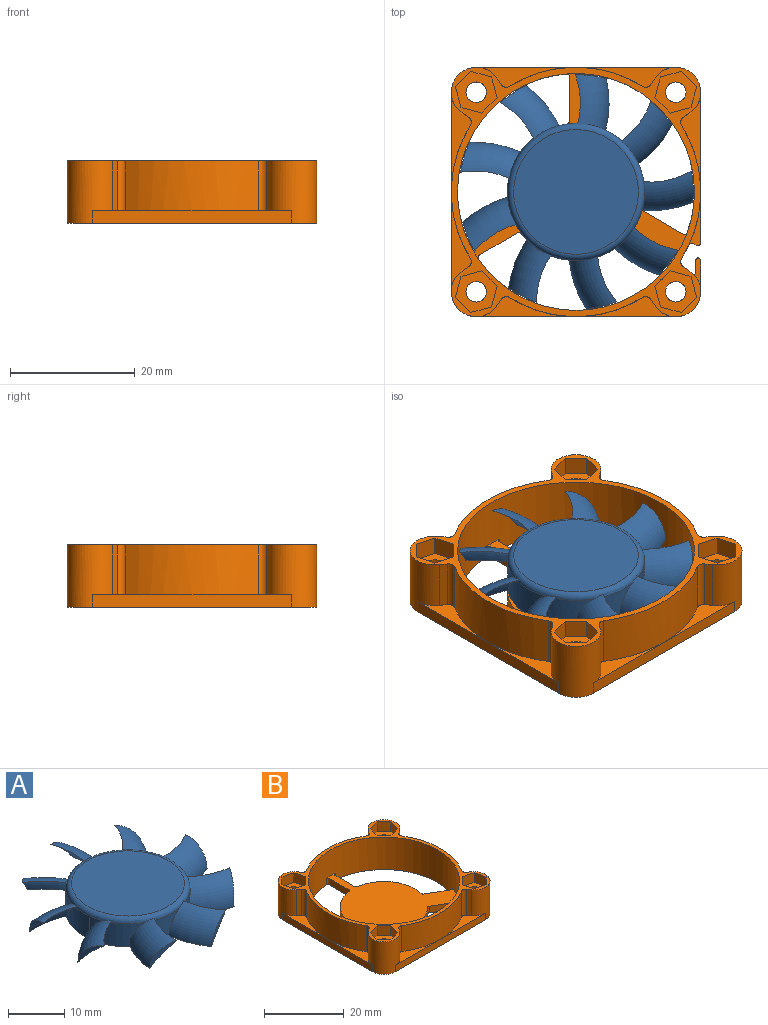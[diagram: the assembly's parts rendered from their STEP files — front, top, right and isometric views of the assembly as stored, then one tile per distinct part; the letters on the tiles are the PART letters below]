
ASSEMBLY  parts=2 mates=1
PART A: 32 faces, bbox 42.3x42.5x6 mm
  f0: cylinder r=11mm len=22mm, axis (0,0,-1), area 307.6mm2, adj f1,f3,f4,f5,f6,f8,f9,f11
  f1: cylinder r=11mm len=4.52mm, axis (0,0,-1), area 3.9mm2, adj f0,f4,f11
  f2: plane 20x20mm, normal (0,0,1), area 314.2mm2, adj f4
  f3: plane 22x22mm, normal (0,0,-1), area 380.1mm2, adj f0
  f4: torus R=10mm, axis (0,0,1), area 102.2mm2, adj f0,f1,f2,f5,f6,f8,f9,f11
  f5: torus R=12.73mm, axis (0,0,-1), area 60.3mm2, adj f0,f4,f6,f7
  f6: torus R=5.4mm, axis (0,0,-1), area 55.4mm2, adj f0,f4,f5,f7
  f7: cylinder r=18.8mm len=4.97mm, axis (0,0,1), area 4.5mm2, adj f5,f6
  f8: torus R=12.73mm, axis (0,0,-1), area 60.3mm2, adj f0,f4,f9,f10
  f9: torus R=5.4mm, axis (0,0,-1), area 55.4mm2, adj f0,f4,f8,f10
  f10: cylinder r=18.8mm len=4.97mm, axis (0,0,1), area 4.5mm2, adj f8,f9
  f11: torus R=12.73mm, axis (0,0,-1), area 60.3mm2, adj f0,f1,f4,f12,f13
  f12: torus R=5.4mm, axis (0,0,-1), area 55.4mm2, adj f0,f4,f11,f13
  f13: cylinder r=18.8mm len=4.97mm, axis (0,0,1), area 4.5mm2, adj f11,f12
  f14: torus R=12.73mm, axis (0,0,-1), area 60.3mm2, adj f0,f4,f15,f16
  f15: torus R=5.4mm, axis (0,0,-1), area 55.4mm2, adj f0,f4,f14,f16
  f16: cylinder r=18.8mm len=4.97mm, axis (0,0,1), area 4.5mm2, adj f14,f15
  f17: torus R=12.73mm, axis (0,0,-1), area 60.3mm2, adj f0,f4,f18,f19
  f18: torus R=5.4mm, axis (0,0,-1), area 55.4mm2, adj f0,f4,f17,f19
  f19: cylinder r=18.8mm len=4.97mm, axis (0,0,1), area 4.5mm2, adj f17,f18
  f20: torus R=12.73mm, axis (0,0,-1), area 60.3mm2, adj f0,f4,f21,f22
  f21: torus R=5.4mm, axis (0,0,-1), area 55.4mm2, adj f0,f4,f20,f22
  f22: cylinder r=18.8mm len=4.99mm, axis (0,0,1), area 4.5mm2, adj f20,f21
  f23: torus R=12.73mm, axis (0,0,-1), area 60.3mm2, adj f0,f4,f24,f25
  f24: torus R=5.4mm, axis (0,0,-1), area 55.4mm2, adj f0,f4,f23,f25
  f25: cylinder r=18.8mm len=4.97mm, axis (0,0,1), area 4.5mm2, adj f23,f24
  f26: torus R=12.73mm, axis (0,0,-1), area 60.3mm2, adj f0,f4,f27,f28
  f27: torus R=5.4mm, axis (0,0,-1), area 55.4mm2, adj f0,f4,f26,f28
  f28: cylinder r=18.8mm len=5mm, axis (0,0,1), area 4.5mm2, adj f26,f27
  f29: torus R=12.73mm, axis (0,0,-1), area 60.3mm2, adj f0,f4,f30,f31
  f30: torus R=5.4mm, axis (0,0,-1), area 55.4mm2, adj f0,f4,f29,f31
  f31: cylinder r=18.8mm len=4.97mm, axis (0,0,1), area 4.5mm2, adj f29,f30
PART B: 115 faces, bbox 40x40x10 mm
  f0: plane 10.28x5.94mm, normal (0.5,0.87,0), area 11.9mm2, adj f19,f33,f35,f80,f81,f82
  f1: plane 2x1.78mm, normal (-1,0,0), area 3.6mm2, adj f8,f33,f81,f97
  f2: plane 16x3.21mm, normal (0,0,1), area 18mm2, adj f26,f27,f56,f57,f100
  f3: plane 16x3.21mm, normal (0,0,1), area 18mm2, adj f25,f26,f65,f69,f106
  f4: plane 16x3.21mm, normal (0,0,1), area 18mm2, adj f21,f22,f34,f60,f102
  f5: plane 16x3.21mm, normal (0,0,1), area 18mm2, adj f23,f24,f62,f63,f104
  f6: plane 16x3.21mm, normal (0,0,1), area 18mm2, adj f27,f28,f57,f58,f101
  f7: plane 35.04x31.24mm, normal (0,0,1), area 457.1mm2, adj f12,f13,f14,f15,f16,f17,f18,f30
  f8: plane 5.45x1.07mm, normal (0,0,1), area 3mm2, adj f1,f28,f29,f81,f96,f97
  f9: plane 16x3.21mm, normal (0,0,1), area 18mm2, adj f22,f23,f61,f62,f103
  f10: plane 8.58x1.89mm, normal (0,0,1), area 5.1mm2, adj f20,f21,f34,f76,f89
  f11: plane 16x3.21mm, normal (0,0,1), area 18mm2, adj f24,f25,f64,f65,f105
  f12: plane 7.04x2mm, normal (1,0,0), area 14.1mm2, adj f7,f33,f87,f92
  f13: cylinder r=19mm len=38mm, axis (0,0,1), area 1168mm2, adj f7,f33,f71,f83,f84,f85,f86,f87
  f14: plane 6.22x3.59mm, normal (0.5,0.87,0), area 14.4mm2, adj f7,f33,f88,f95
  f15: plane 6.09x3.52mm, normal (0.5,-0.87,0), area 14.1mm2, adj f7,f33,f84,f90
  f16: cylinder r=11mm len=16.31mm, axis (0,0,1), area 36.9mm2, adj f7,f33,f90,f94
  f17: plane 6.09x3.52mm, normal (-0.5,0.87,0), area 14.1mm2, adj f7,f33,f85,f91
  f18: plane 7.04x2mm, normal (-1,0,0), area 14.1mm2, adj f7,f33,f86,f93
  f19: cylinder r=11mm len=3.9mm, axis (0,0,1), area 4.4mm2, adj f0,f20,f33,f35,f77
  f20: plane 8.8x5.08mm, normal (-0.5,-0.87,0), area 6.1mm2, adj f10,f19,f33,f76,f77,f78,f89
  f21: plane 24.08x2mm, normal (1,0,0), area 48.2mm2, adj f4,f10,f22,f33,f89
  f22: cylinder r=4mm len=10mm, axis (0,0,1), area 124.5mm2, adj f4,f9,f21,f23,f33,f60,f61,f71
  f23: plane 32x2mm, normal (0,1,0), area 64mm2, adj f5,f9,f22,f24,f33
  f24: cylinder r=4mm len=10mm, axis (0,0,1), area 124.5mm2, adj f5,f11,f23,f25,f33,f63,f64,f71
  f25: plane 32x2mm, normal (-1,0,0), area 64mm2, adj f3,f11,f24,f26,f33
  f26: cylinder r=4mm len=10mm, axis (0,0,1), area 124.5mm2, adj f2,f3,f25,f27,f33,f56,f69,f71
  f27: plane 32x2mm, normal (0,-1,0), area 64mm2, adj f2,f6,f26,f28,f33
  f28: cylinder r=4mm len=10mm, axis (0,0,1), area 124.9mm2, adj f6,f8,f27,f29,f33,f58,f59,f71
  f29: plane 4.96x2mm, normal (1,0,0), area 9.9mm2, adj f8,f28,f33,f96
  f30: plane 6.22x3.59mm, normal (-0.5,-0.87,0), area 14.4mm2, adj f7,f33,f83,f94
  f31: cylinder r=11mm len=15.12mm, axis (0,0,1), area 40.3mm2, adj f7,f33,f91,f93
  f32: cylinder r=11mm len=13.49mm, axis (0,0,1), area 36.9mm2, adj f7,f33,f92,f95
  f33: plane 40x40mm, normal (0,0,-1), area 793.4mm2, adj f0,f1,f12,f13,f14,f15,f16,f17
  f34: cylinder r=20mm len=21.25mm, axis (0,0,1), area 180.4mm2, adj f4,f10,f71,f76,f79,f98,f102
  f35: plane 9.49x8.4mm, normal (0,0,-1), area 34.2mm2, adj f0,f19,f77,f79,f80
  f36: plane 3.35x3mm, normal (-0.26,-0.97,0), area 10.4mm2, adj f37,f70,f71,f75
  f37: plane 3.35x3mm, normal (-0.97,-0.26,0), area 10.4mm2, adj f36,f38,f71,f75
  f38: plane 3x2.45mm, normal (-0.71,0.71,0), area 10.4mm2, adj f37,f39,f71,f75
  f39: plane 3.35x3mm, normal (0.26,0.97,0), area 10.4mm2, adj f38,f40,f71,f75
  f40: plane 3.35x3mm, normal (0.97,0.26,0), area 10.4mm2, adj f39,f70,f71,f75
  f41: plane 3x2.45mm, normal (-0.71,0.71,0), area 10.4mm2, adj f42,f66,f71,f73
  f42: plane 3.35x3mm, normal (0.26,0.97,0), area 10.4mm2, adj f41,f43,f71,f73
  f43: plane 3.35x3mm, normal (0.97,0.26,0), area 10.4mm2, adj f42,f44,f71,f73
  f44: plane 3x2.45mm, normal (0.71,-0.71,0), area 10.4mm2, adj f43,f45,f71,f73
  f45: plane 3.35x3mm, normal (-0.26,-0.97,0), area 10.4mm2, adj f44,f66,f71,f73
  f46: plane 3.35x3mm, normal (-0.97,0.26,0), area 10.4mm2, adj f47,f67,f71,f72
  f47: plane 3.35x3mm, normal (-0.26,0.97,0), area 10.4mm2, adj f46,f48,f71,f72
  f48: plane 3x2.45mm, normal (0.71,0.71,0), area 10.4mm2, adj f47,f49,f71,f72
  f49: plane 3.35x3mm, normal (0.97,-0.26,0), area 10.4mm2, adj f48,f50,f71,f72
  f50: plane 3.35x3mm, normal (0.26,-0.97,0), area 10.4mm2, adj f49,f67,f71,f72
  f51: plane 3x2.45mm, normal (-0.71,-0.71,0), area 10.4mm2, adj f52,f68,f71,f74
  f52: plane 3.35x3mm, normal (-0.97,0.26,0), area 10.4mm2, adj f51,f53,f71,f74
  f53: plane 3.35x3mm, normal (-0.26,0.97,0), area 10.4mm2, adj f52,f54,f71,f74
  f54: plane 3x2.45mm, normal (0.71,0.71,0), area 10.4mm2, adj f53,f55,f71,f74
  f55: plane 3.35x3mm, normal (0.97,-0.26,0), area 10.4mm2, adj f54,f68,f71,f74
  f56: plane 8x1.06mm, normal (0.82,-0.57,0), area 10.4mm2, adj f2,f26,f71,f100
  f57: cylinder r=20mm len=21.25mm, axis (0,0,-1), area 179.2mm2, adj f2,f6,f71,f100,f101
  f58: plane 8x1.06mm, normal (-0.82,-0.57,0), area 10.4mm2, adj f6,f28,f71,f101
  f59: plane 8.5x1.06mm, normal (0.57,0.82,0), area 11mm2, adj f28,f71,f80,f98
  f60: plane 8x1.06mm, normal (0.57,-0.82,0), area 10.4mm2, adj f4,f22,f71,f102
  f61: plane 8x1.06mm, normal (-0.82,0.57,0), area 10.4mm2, adj f9,f22,f71,f103
  f62: cylinder r=20mm len=21.25mm, axis (0,0,-1), area 179.2mm2, adj f5,f9,f71,f103,f104
  f63: plane 8x1.06mm, normal (0.82,0.57,0), area 10.4mm2, adj f5,f24,f71,f104
  f64: plane 8x1.06mm, normal (-0.57,-0.82,0), area 10.4mm2, adj f11,f24,f71,f105
  f65: cylinder r=20mm len=21.25mm, axis (0,0,-1), area 179.2mm2, adj f3,f11,f71,f105,f106
  f66: plane 3.35x3mm, normal (-0.97,-0.26,0), area 10.4mm2, adj f41,f45,f71,f73
  f67: plane 3x2.45mm, normal (-0.71,-0.71,0), area 10.4mm2, adj f46,f50,f71,f72
  f68: plane 3.35x3mm, normal (0.26,-0.97,0), area 10.4mm2, adj f51,f55,f71,f74
  f69: plane 8x1.06mm, normal (-0.57,0.82,0), area 10.4mm2, adj f3,f26,f71,f106
  f70: plane 3x2.45mm, normal (0.71,-0.71,0), area 10.4mm2, adj f36,f40,f71,f75
  f71: plane 40x40mm, normal (0,0,1), area 183.3mm2, adj f13,f22,f24,f26,f28,f34,f36,f37
  f72: plane 6.69x6.69mm, normal (0,0,1), area 22.6mm2, adj f46,f47,f48,f49,f50,f67,f111
  f73: plane 6.69x6.69mm, normal (0,0,1), area 22.6mm2, adj f41,f42,f43,f44,f45,f66,f109
  f74: plane 6.69x6.69mm, normal (0,0,1), area 22.6mm2, adj f51,f52,f53,f54,f55,f68,f107
  f75: plane 6.69x6.69mm, normal (0,0,1), area 22.6mm2, adj f36,f37,f38,f39,f40,f70,f113
  f76: cylinder r=0.5mm len=0.7mm, axis (0,0,1), area 0.4mm2, adj f10,f20,f34,f78
  f77: cylinder r=0.5mm len=7.74mm, axis (0.87,-0.5,0), area 6.8mm2, adj f19,f20,f35,f78
  f78: bspline ~1.22x1.19mm, area 0.9mm2, adj f20,f76,f77,f79
  f79: torus R=19.5mm, axis (0,0,1), area 2.5mm2, adj f34,f35,f78,f99
  f80: cylinder r=0.5mm len=2.57mm, axis (0.82,-0.57,0), area 1.5mm2, adj f0,f35,f59,f82,f99
  f81: cylinder r=0.5mm len=2mm, axis (0,0,-1), area 1.7mm2, adj f0,f1,f8,f28,f33,f82
  f82: torus R=3.5mm, axis (0,0,1), area 0.4mm2, adj f0,f28,f80,f81
  f83: cylinder r=0.5mm len=2mm, axis (0,0,1), area 1.7mm2, adj f7,f13,f30,f33
  f84: cylinder r=0.5mm len=2mm, axis (0,0,1), area 1.7mm2, adj f7,f13,f15,f33
  f85: cylinder r=0.5mm len=2mm, axis (0,0,1), area 1.7mm2, adj f7,f13,f17,f33
  f86: cylinder r=0.5mm len=2mm, axis (0,0,1), area 1.7mm2, adj f7,f13,f18,f33
  f87: cylinder r=0.5mm len=2mm, axis (0,0,1), area 1.7mm2, adj f7,f12,f13,f33
  f88: cylinder r=0.5mm len=2mm, axis (0,0,1), area 1.7mm2, adj f7,f13,f14,f33
  f89: cylinder r=0.5mm len=2mm, axis (0,0,-1), area 2.1mm2, adj f10,f20,f21,f33
  f90: cylinder r=0.5mm len=2mm, axis (0,0,1), area 1.4mm2, adj f7,f15,f16,f33
  f91: cylinder r=0.5mm len=2mm, axis (0,0,1), area 1.4mm2, adj f7,f17,f31,f33
  f92: cylinder r=0.5mm len=2mm, axis (0,0,1), area 1.4mm2, adj f7,f12,f32,f33
  f93: cylinder r=0.5mm len=2mm, axis (0,0,1), area 1.4mm2, adj f7,f18,f31,f33
  f94: cylinder r=0.5mm len=2mm, axis (0,0,1), area 1.3mm2, adj f7,f16,f30,f33
  f95: cylinder r=0.5mm len=2mm, axis (0,0,1), area 1.3mm2, adj f7,f14,f32,f33
  f96: cylinder r=0.5mm len=2mm, axis (0,0,1), area 1.4mm2, adj f8,f29,f33,f97
  f97: cylinder r=0.5mm len=2mm, axis (0,0,1), area 1.4mm2, adj f1,f8,f33,f96
  f98: cylinder r=1mm len=8.5mm, axis (0,0,1), area 12.9mm2, adj f34,f59,f71,f99
  f99: bspline ~1.5x1.35mm, area 0.5mm2, adj f79,f80,f98
  f100: cylinder r=1mm len=8mm, axis (0,0,-1), area 12.2mm2, adj f2,f56,f57,f71
  f101: cylinder r=1mm len=8mm, axis (0,0,-1), area 12.2mm2, adj f6,f57,f58,f71
  f102: cylinder r=1mm len=8mm, axis (0,0,1), area 12.2mm2, adj f4,f34,f60,f71
  f103: cylinder r=1mm len=8mm, axis (0,0,-1), area 12.2mm2, adj f9,f61,f62,f71
  f104: cylinder r=1mm len=8mm, axis (0,0,-1), area 12.2mm2, adj f5,f62,f63,f71
  f105: cylinder r=1mm len=8mm, axis (0,0,-1), area 12.2mm2, adj f11,f64,f65,f71
  f106: cylinder r=1mm len=8mm, axis (0,0,-1), area 12.2mm2, adj f3,f65,f69,f71
  f107: cylinder r=1.65mm len=6.4mm, axis (0,0,-1), area 66.4mm2, adj f74,f108
  f108: cone r=1.65mm half-angle=45deg, axis (0,0,-1), area 10.4mm2, adj f33,f107
  f109: cylinder r=1.65mm len=6.4mm, axis (0,0,-1), area 66.4mm2, adj f73,f110
  f110: cone r=1.65mm half-angle=45deg, axis (0,0,-1), area 10.4mm2, adj f33,f109
  f111: cylinder r=1.65mm len=6.4mm, axis (0,0,-1), area 66.4mm2, adj f72,f112
  f112: cone r=1.65mm half-angle=45deg, axis (0,0,-1), area 10.4mm2, adj f33,f111
  f113: cylinder r=1.65mm len=6.4mm, axis (0,0,-1), area 66.4mm2, adj f75,f114
  f114: cone r=1.65mm half-angle=45deg, axis (0,0,-1), area 10.4mm2, adj f33,f113
PLACE A rot(axis=(0,0,-1),81.8deg) t=(0,0,0)mm
PLACE B at identity fixed
MATE revolute A.f0 <-> B.f13  axis (0,0,-1) through (0,0,0)mm
